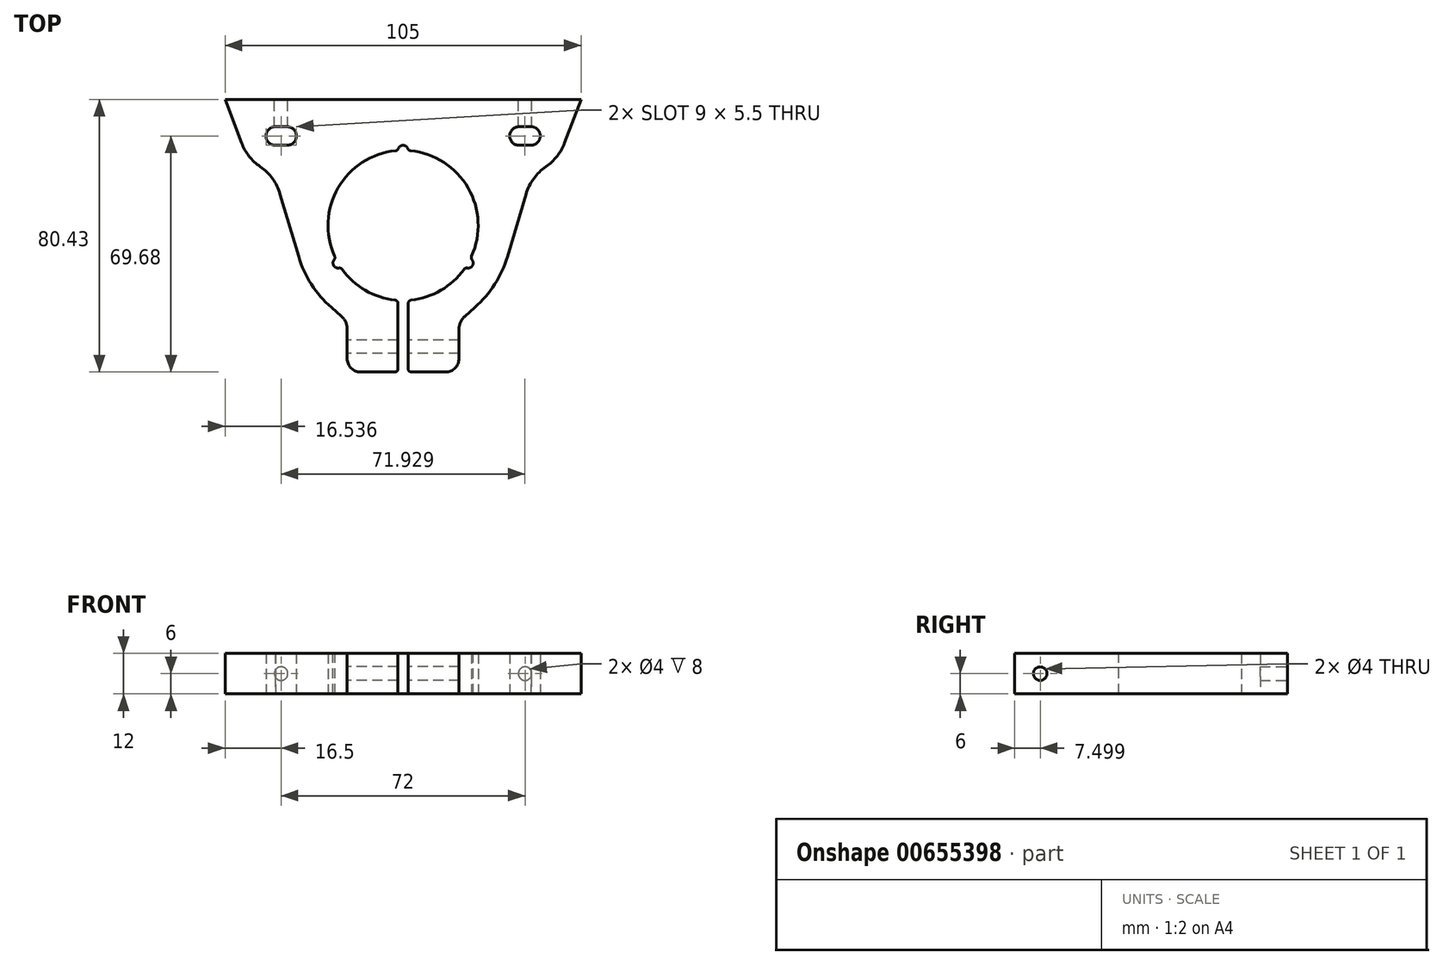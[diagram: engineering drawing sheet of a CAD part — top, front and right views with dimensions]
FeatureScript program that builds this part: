
annotation { "Feature Type Name" : "Feature", "Feature Type Description" : "" }
export const myFeature = defineFeature(function(context is Context, id is Id, definition is map)
    precondition{}
    {
        {
            var Q0;
            Q0=qCreatedBy(makeId("Top.planeOp"),FACE);
            var sketch = newSketch(context, id + "F0", { "sketchPlane" : qUnion([Q0])});
            skLineSegment(sketch, "E0", {"start": v(-52.5, 0) * mm, "end": v(52.5, 0) * mm});
            skLineSegment(sketch, "E1", {"start": v(-21.17, -61.35) * mm, "end": v(-16.5, -65.43) * mm});
            skLineSegment(sketch, "E2", {"start": v(-16.5, -65.43) * mm, "end": v(-16.5, -80.43) * mm});
            skLineSegment(sketch, "E3", {"start": v(-16.5, -80.43) * mm, "end": v(-1.5, -80.43) * mm});
            skLineSegment(sketch, "E4", {"start": v(-1.5, -80.43) * mm, "end": v(-1.5, -59.25) * mm});
            skArc(sketch, "E5", {"start": v(1.5, -59.25) * mm, "mid": v(0, -15) * mm, "end": v(-1.5, -59.25) * mm});
            skLineSegment(sketch, "E6.MirrorCS", {"start": v(16.5, -65.43) * mm, "end": v(16.5, -80.43) * mm});
            skLineSegment(sketch, "E7.MirrorCS", {"start": v(16.5, -80.43) * mm, "end": v(1.5, -80.43) * mm});
            skLineSegment(sketch, "E8.MirrorCS", {"start": v(1.5, -80.43) * mm, "end": v(1.5, -59.25) * mm});
            skCircle(sketch, "E9", {"center": v(0, -37.15) * mm, "radius": 32.15 * mm, "construction": true});
            skLineSegment(sketch, "E10", {"start": v(0, -37.15) * mm, "end": v(-21.17, -61.35) * mm, "construction": true});
            skLineSegment(sketch, "E11.bottom", {"start": v(-37.64, -13.5) * mm, "end": v(-34.21, -13.5) * mm});
            skLineSegment(sketch, "E11.top", {"start": v(-37.79, -8) * mm, "end": v(-34.21, -8) * mm});
            skArc(sketch, "E12", {"start": v(-37.79, -8) * mm, "mid": v(-40.46, -10.82) * mm, "end": v(-37.64, -13.5) * mm});
            skArc(sketch, "E13", {"start": v(-34.21, -13.5) * mm, "mid": v(-31.46, -10.75) * mm, "end": v(-34.21, -8) * mm});
            skLineSegment(sketch, "E14", {"start": v(0, 0) * mm, "end": v(0, -15) * mm, "construction": true});
            skLineSegment(sketch, "E15.MirrorCS", {"start": v(37.64, -13.5) * mm, "end": v(34.21, -13.5) * mm});
            skArc(sketch, "E16.MirrorCS", {"start": v(34.21, -13.5) * mm, "mid": v(31.46, -10.75) * mm, "end": v(34.21, -8) * mm});
            skArc(sketch, "E17.MirrorCS", {"start": v(37.79, -8) * mm, "mid": v(40.46, -10.82) * mm, "end": v(37.64, -13.5) * mm});
            skLineSegment(sketch, "E18.MirrorCS", {"start": v(37.79, -8) * mm, "end": v(34.21, -8) * mm});
            skArc(sketch, "E19.0", {"start": v(-47.67, -12.75) * mm, "mid": v(-45.45, -16.69) * mm, "end": v(-42.16, -19.79) * mm});
            skLineSegment(sketch, "E20", {"start": v(-52.5, 0) * mm, "end": v(-47.67, -12.75) * mm});
            skLineSegment(sketch, "E21", {"start": v(-36.3, -27.87) * mm, "end": v(-30.82, -46.3) * mm});
            skArc(sketch, "E22.MirrorCS", {"start": v(47.67, -12.75) * mm, "mid": v(45.45, -16.69) * mm, "end": v(42.16, -19.79) * mm});
            skLineSegment(sketch, "E23.MirrorCS", {"start": v(52.5, 0) * mm, "end": v(47.67, -12.75) * mm});
            skArc(sketch, "E24", {"start": v(-21.17, -61.35) * mm, "mid": v(-27.06, -54.5) * mm, "end": v(-30.82, -46.3) * mm});
            skLineSegment(sketch, "E25.MirrorCS", {"start": v(36.3, -27.87) * mm, "end": v(30.82, -46.3) * mm});
            skArc(sketch, "E26.MirrorCS", {"start": v(21.17, -61.35) * mm, "mid": v(27.06, -54.5) * mm, "end": v(30.82, -46.3) * mm});
            skLineSegment(sketch, "E27.MirrorCS", {"start": v(21.17, -61.35) * mm, "end": v(16.5, -65.43) * mm});
            skPoint(sketch, "E28.visualSharp", {"position": v(-38.1, -21.76) * mm});
            skArc(sketch, "E28.filletArc", {"start": v(-36.3, -27.87) * mm, "mid": v(-38.53, -23.32) * mm, "end": v(-42.16, -19.79) * mm});
            skPoint(sketch, "E29.visualSharp", {"position": v(38.1, -21.76) * mm});
            skArc(sketch, "E29.filletArc", {"start": v(42.16, -19.79) * mm, "mid": v(38.53, -23.32) * mm, "end": v(36.3, -27.87) * mm});
            skSolve(sketch);
        }
        {
            var Q0;
            Q0=qSketchRegion(id+"F0",true);
            extrude(context, id + "F1", {"entities" : qUnion([Q0]), "depth" : 12 * mm, "offsetDistance" : 25 * mm});
        }
        {
            var Q0;
            Q0=makeQuery(id+"F1.opExtrude","SWEPT_EDGE",EDGE,{"disambiguationData":[OSD([sQuery(id+"F0.wireOp",EDGE,"E1"),sQuery(id+"F0.wireOp",EDGE,"E2")])]});
            var Q1;
            Q1=makeQuery(id+"F1.opExtrude","SWEPT_EDGE",EDGE,{"disambiguationData":[OSD([sQuery(id+"F0.wireOp",EDGE,"E6.MirrorCS"),sQuery(id+"F0.wireOp",EDGE,"E27.MirrorCS")])]});
            fillet(context, id + "F2", {"entities" : qUnion([Q0, Q1]), "radius" : 5 * mm, "tangentPropagation" : true, "allowEdgeOverflow" : false});
        }
        {
            var Q0;
            Q0=makeQuery(id+"F1.opExtrude","SWEPT_FACE",FACE,{"disambiguationData":[OSD([sQuery(id+"F0.wireOp",EDGE,"E2")])]});
            var sketch = newSketch(context, id + "F3", { "sketchPlane" : qUnion([Q0])});
            skCircle(sketch, "E30", {"center": v(72.93, 6) * mm, "radius": 2 * mm});
            skPoint(sketch, "E30.centerSnap0", {"position": v(80.43, 6) * mm});
            skSolve(sketch);
        }
        {
            var Q0;
            Q0=qSketchRegion(id+"F3",true);
            extrude(context, id + "F4", {"entities" : qUnion([Q0]), "operationType" : NewBodyOperationType.REMOVE, "endBound" : BoundingType.THROUGH_ALL, "oppositeDirection" : true, "depth" : 25 * mm, "offsetDistance" : 25 * mm});
        }
        {
            var Q0;
            Q0=makeQuery(id+"F1.opExtrude","SWEPT_EDGE",EDGE,{"disambiguationData":[OSD([sQuery(id+"F0.wireOp",EDGE,"E1"),sQuery(id+"F0.wireOp",EDGE,"E2")])]});
            var Q1;
            Q1=makeQuery(id+"F1.opExtrude","SWEPT_EDGE",EDGE,{"disambiguationData":[OSD([sQuery(id+"F0.wireOp",EDGE,"E2"),sQuery(id+"F0.wireOp",EDGE,"E3")])]});
            var Q2;
            Q2=makeQuery(id+"F1.opExtrude","SWEPT_EDGE",EDGE,{"disambiguationData":[OSD([sQuery(id+"F0.wireOp",EDGE,"E6.MirrorCS"),sQuery(id+"F0.wireOp",EDGE,"E7.MirrorCS")])]});
            var Q3;
            Q3=makeQuery(id+"F1.opExtrude","SWEPT_EDGE",EDGE,{"disambiguationData":[OSD([sQuery(id+"F0.wireOp",EDGE,"6f19a3d9-82da-4a62-acf6-6007c0667a970.MirrorCS"),sQuery(id+"F0.wireOp",EDGE,"E6.MirrorCS")])]});
            fillet(context, id + "F5", {"entities" : qUnion([Q0, Q1, Q2, Q3]), "radius" : 4 * mm, "tangentPropagation" : true, "allowEdgeOverflow" : false});
        }
        {
            var Q0;
            Q0=makeQuery(id+"F1.opExtrude","SWEPT_FACE",FACE,{"disambiguationData":[OSD([sQuery(id+"F0.wireOp",EDGE,"E0")])]});
            var sketch = newSketch(context, id + "F6", { "sketchPlane" : qUnion([Q0])});
            skCircle(sketch, "E31", {"center": v(-36, 6) * mm, "radius": 2 * mm});
            skPoint(sketch, "E31.centerSnap0", {"position": v(-52.5, 6) * mm});
            skCircle(sketch, "E32", {"center": v(36, 6) * mm, "radius": 2 * mm});
            skSolve(sketch);
        }
        {
            var Q0;
            Q0=qSketchRegion(id+"F6",true);
            extrude(context, id + "F7", {"entities" : qUnion([Q0]), "operationType" : NewBodyOperationType.REMOVE, "oppositeDirection" : true, "depth" : 12 * mm, "offsetDistance" : 25 * mm});
        }
        {
            var Q0;
            Q0=makeQuery(id+"F1.opExtrude","CAP_FACE",FACE,{"disambiguationData":[OSD([sQuery(id+"F0.wireOp",EDGE,"E0"),sQuery(id+"F0.wireOp",EDGE,"E1"),sQuery(id+"F0.wireOp",EDGE,"E2"),sQuery(id+"F0.wireOp",EDGE,"E3"),sQuery(id+"F0.wireOp",EDGE,"E4"),sQuery(id+"F0.wireOp",EDGE,"E5"),sQuery(id+"F0.wireOp",EDGE,"E6.MirrorCS"),sQuery(id+"F0.wireOp",EDGE,"E7.MirrorCS"),sQuery(id+"F0.wireOp",EDGE,"E8.MirrorCS"),sQuery(id+"F0.wireOp",EDGE,"E11.bottom"),sQuery(id+"F0.wireOp",EDGE,"E11.top"),sQuery(id+"F0.wireOp",EDGE,"E12"),sQuery(id+"F0.wireOp",EDGE,"E13"),sQuery(id+"F0.wireOp",EDGE,"E15.MirrorCS"),sQuery(id+"F0.wireOp",EDGE,"E16.MirrorCS"),sQuery(id+"F0.wireOp",EDGE,"E17.MirrorCS"),sQuery(id+"F0.wireOp",EDGE,"E18.MirrorCS"),sQuery(id+"F0.wireOp",EDGE,"E19.0"),sQuery(id+"F0.wireOp",EDGE,"E20"),sQuery(id+"F0.wireOp",EDGE,"E21"),sQuery(id+"F0.wireOp",EDGE,"E22.MirrorCS"),sQuery(id+"F0.wireOp",EDGE,"E23.MirrorCS"),sQuery(id+"F0.wireOp",EDGE,"E24"),sQuery(id+"F0.wireOp",EDGE,"E25.MirrorCS"),sQuery(id+"F0.wireOp",EDGE,"E26.MirrorCS"),sQuery(id+"F0.wireOp",EDGE,"E27.MirrorCS"),sQuery(id+"F0.wireOp",EDGE,"E28.filletArc"),sQuery(id+"F0.wireOp",EDGE,"E29.filletArc")])],"isStart":false});
            var sketch = newSketch(context, id + "F8", { "sketchPlane" : qUnion([Q0])});
            skCircle(sketch, "E33", {"center": v(0, -15) * mm, "radius": 1.5 * mm});
            skCircle(sketch, "E34.1.0", {"center": v(-19.18, -48.22) * mm, "radius": 1.5 * mm});
            skCircle(sketch, "E34.2.0", {"center": v(19.18, -48.23) * mm, "radius": 1.5 * mm});
            skPoint(sketch, "E34.center", {"position": v(0, -37.15) * mm});
            skSolve(sketch);
        }
        {
            var Q0;
            Q0=qSketchRegion(id+"F8",true);
            extrude(context, id + "F9", {"entities" : qUnion([Q0]), "operationType" : NewBodyOperationType.REMOVE, "oppositeDirection" : true, "depth" : 25 * mm, "offsetDistance" : 25 * mm});
        }
        {
            var Q0;
            Q0=makeQuery(id+"F9.boolean.opBoolean","INTERSECT",EDGE,{"disambiguationData":[OD(1.0)],"derivedFrom":[makeQuery(id+"F1.opExtrude","SWEPT_FACE",FACE,{"disambiguationData":[OSD([sQuery(id+"F0.wireOp",EDGE,"E5")])]}),makeQuery(id+"F9.opExtrude","SWEPT_FACE",FACE,{"disambiguationData":[OSD([sQuery(id+"F8.wireOp",EDGE,"E33")])]})]});
            var Q1;
            Q1=makeQuery(id+"F9.boolean.opBoolean","INTERSECT",EDGE,{"disambiguationData":[OD(0.0)],"derivedFrom":[makeQuery(id+"F1.opExtrude","SWEPT_FACE",FACE,{"disambiguationData":[OSD([sQuery(id+"F0.wireOp",EDGE,"E5")])]}),makeQuery(id+"F9.opExtrude","SWEPT_FACE",FACE,{"disambiguationData":[OSD([sQuery(id+"F8.wireOp",EDGE,"E33")])]})]});
            var Q2;
            Q2=makeQuery(id+"F9.boolean.opBoolean","INTERSECT",EDGE,{"disambiguationData":[OD(1.0)],"derivedFrom":[makeQuery(id+"F1.opExtrude","SWEPT_FACE",FACE,{"disambiguationData":[OSD([sQuery(id+"F0.wireOp",EDGE,"E5")])]}),makeQuery(id+"F9.opExtrude","SWEPT_FACE",FACE,{"disambiguationData":[OSD([sQuery(id+"F8.wireOp",EDGE,"E34.1.0")])]})]});
            var Q3;
            Q3=makeQuery(id+"F9.boolean.opBoolean","INTERSECT",EDGE,{"disambiguationData":[OD(0.0)],"derivedFrom":[makeQuery(id+"F1.opExtrude","SWEPT_FACE",FACE,{"disambiguationData":[OSD([sQuery(id+"F0.wireOp",EDGE,"E5")])]}),makeQuery(id+"F9.opExtrude","SWEPT_FACE",FACE,{"disambiguationData":[OSD([sQuery(id+"F8.wireOp",EDGE,"E34.1.0")])]})]});
            var Q4;
            Q4=makeQuery(id+"F9.boolean.opBoolean","INTERSECT",EDGE,{"disambiguationData":[OD(0.0)],"derivedFrom":[makeQuery(id+"F1.opExtrude","SWEPT_FACE",FACE,{"disambiguationData":[OSD([sQuery(id+"F0.wireOp",EDGE,"E5")])]}),makeQuery(id+"F9.opExtrude","SWEPT_FACE",FACE,{"disambiguationData":[OSD([sQuery(id+"F8.wireOp",EDGE,"E34.2.0")])]})]});
            var Q5;
            Q5=makeQuery(id+"F9.boolean.opBoolean","INTERSECT",EDGE,{"disambiguationData":[OD(1.0)],"derivedFrom":[makeQuery(id+"F1.opExtrude","SWEPT_FACE",FACE,{"disambiguationData":[OSD([sQuery(id+"F0.wireOp",EDGE,"E5")])]}),makeQuery(id+"F9.opExtrude","SWEPT_FACE",FACE,{"disambiguationData":[OSD([sQuery(id+"F8.wireOp",EDGE,"E34.2.0")])]})]});
            var Q6;
            Q6=makeQuery(id+"F1.opExtrude","SWEPT_EDGE",EDGE,{"disambiguationData":[OSD([sQuery(id+"F0.wireOp",EDGE,"E5"),sQuery(id+"F0.wireOp",EDGE,"E8.MirrorCS")])]});
            var Q7;
            Q7=makeQuery(id+"F1.opExtrude","SWEPT_EDGE",EDGE,{"disambiguationData":[OSD([sQuery(id+"F0.wireOp",EDGE,"E4"),sQuery(id+"F0.wireOp",EDGE,"E5")])]});
            var Q8;
            Q8=makeQuery(id+"F1.opExtrude","SWEPT_EDGE",EDGE,{"disambiguationData":[OSD([sQuery(id+"F0.wireOp",EDGE,"E7.MirrorCS"),sQuery(id+"F0.wireOp",EDGE,"E8.MirrorCS")])]});
            var Q9;
            Q9=makeQuery(id+"F1.opExtrude","SWEPT_EDGE",EDGE,{"disambiguationData":[OSD([sQuery(id+"F0.wireOp",EDGE,"E3"),sQuery(id+"F0.wireOp",EDGE,"E4")])]});
            fillet(context, id + "F10", {"entities" : qUnion([Q0, Q1, Q2, Q3, Q4, Q5, Q6, Q7, Q8, Q9]), "radius" : 1 * mm, "tangentPropagation" : true, "allowEdgeOverflow" : false});
        }
    });
